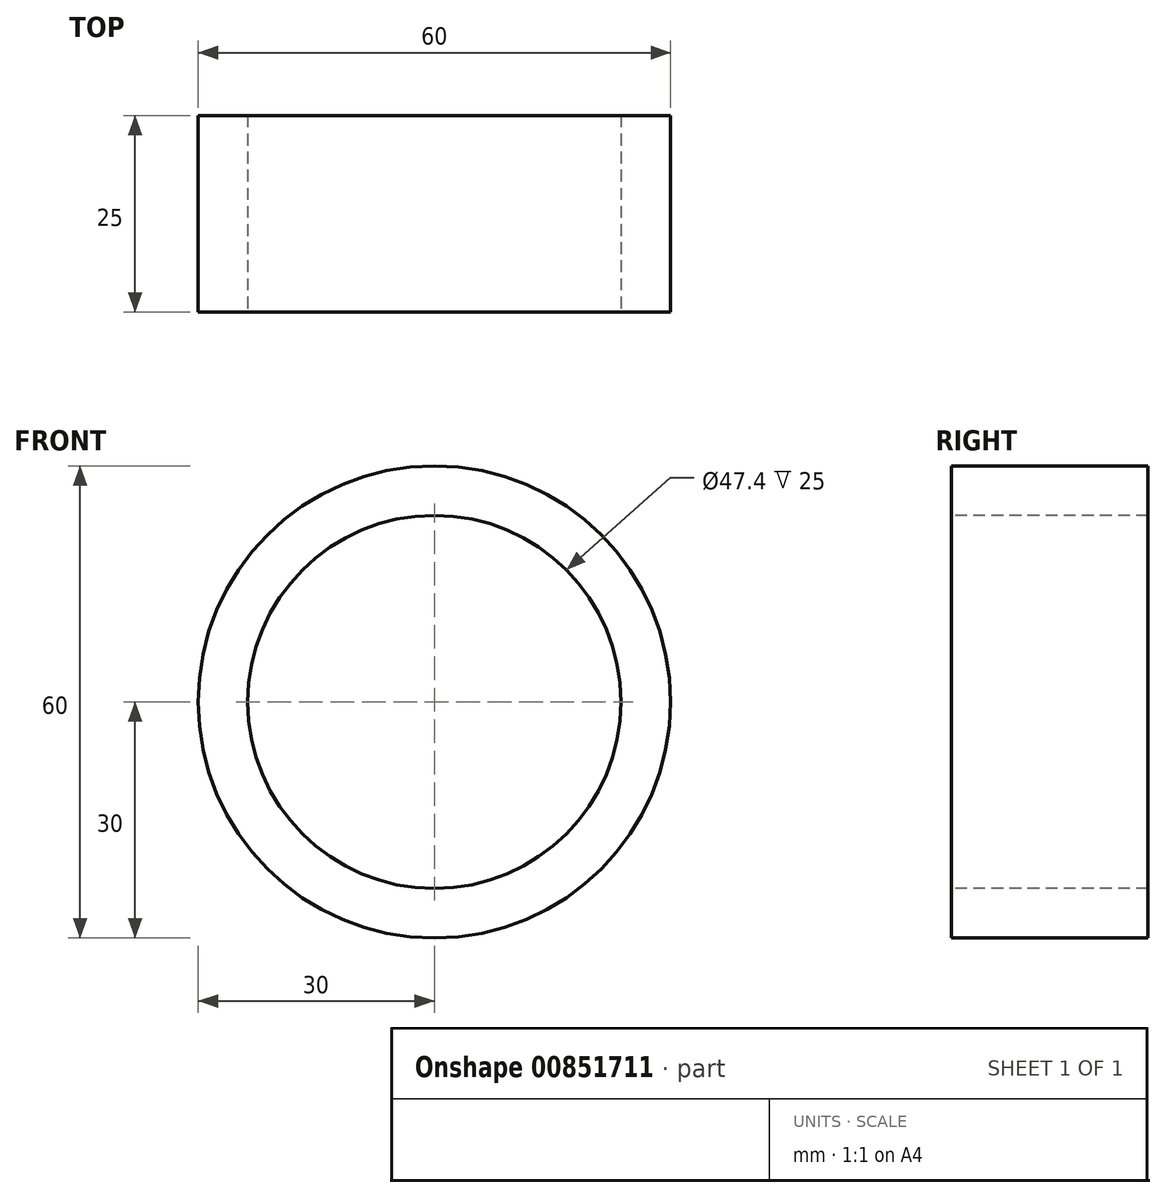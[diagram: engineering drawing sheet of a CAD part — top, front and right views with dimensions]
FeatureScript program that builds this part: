
annotation { "Feature Type Name" : "Feature", "Feature Type Description" : "" }
export const myFeature = defineFeature(function(context is Context, id is Id, definition is map)
    precondition{}
    {
        {
            var Q0;
            Q0=qCreatedBy(makeId("Front.planeOp"),FACE);
            var sketch = newSketch(context, id + "F0", { "sketchPlane" : qUnion([Q0])});
            skCircle(sketch, "E0", {"center": v(0, 0) * mm, "radius": 30 * mm});
            skSolve(sketch);
        }
        {
            var Q0;
            Q0=makeQuery(id+"F0.imprint","IMPRINT",FACE,{"disambiguationData":[TD([[makeQuery(id+"F0.imprint","IMPRINT",EDGE,{"derivedFrom":sQuery(id+"F0.wireOp",EDGE,"E0")}),1.0]])]});
            extrude(context, id + "F1", {"entities" : qUnion([Q0]), "depth" : 25 * mm, "offsetDistance" : 25 * mm});
        }
        {
            var Q0;
            Q0=makeQuery(id+"F1.opExtrude","CAP_FACE",FACE,{"disambiguationData":[OSD([sQuery(id+"F0.wireOp",EDGE,"E0")])],"isStart":false});
            var sketch = newSketch(context, id + "F2", { "sketchPlane" : qUnion([Q0])});
            skSolve(sketch);
        }
        {
            var Q0;
            Q0=makeQuery(id+"F2.imprint","IMPRINT",FACE,{"disambiguationData":[TD([[makeQuery(id+"F2.imprint","IMPRINT",EDGE,{"derivedFrom":makeQuery(id+"F1.opExtrude","CAP_EDGE",EDGE,{"disambiguationData":[OSD([sQuery(id+"F0.wireOp",EDGE,"E0")])],"isStart":false})}),1.0]])]});
            var sketch = newSketch(context, id + "F3", { "sketchPlane" : qUnion([Q0])});
            skCircle(sketch, "E1", {"center": v(0, 0) * mm, "radius": 23.7 * mm});
            skSolve(sketch);
        }
        {
            var Q0;
            Q0 = qSketchRegion(id + "F3", true);
            extrude(context, id + "F4", {"entities" : qUnion([Q0]), "operationType" : NewBodyOperationType.REMOVE, "endBound" : BoundingType.THROUGH_ALL, "oppositeDirection" : true, "depth" : 25 * mm, "offsetDistance" : 25 * mm});
        }
    });
